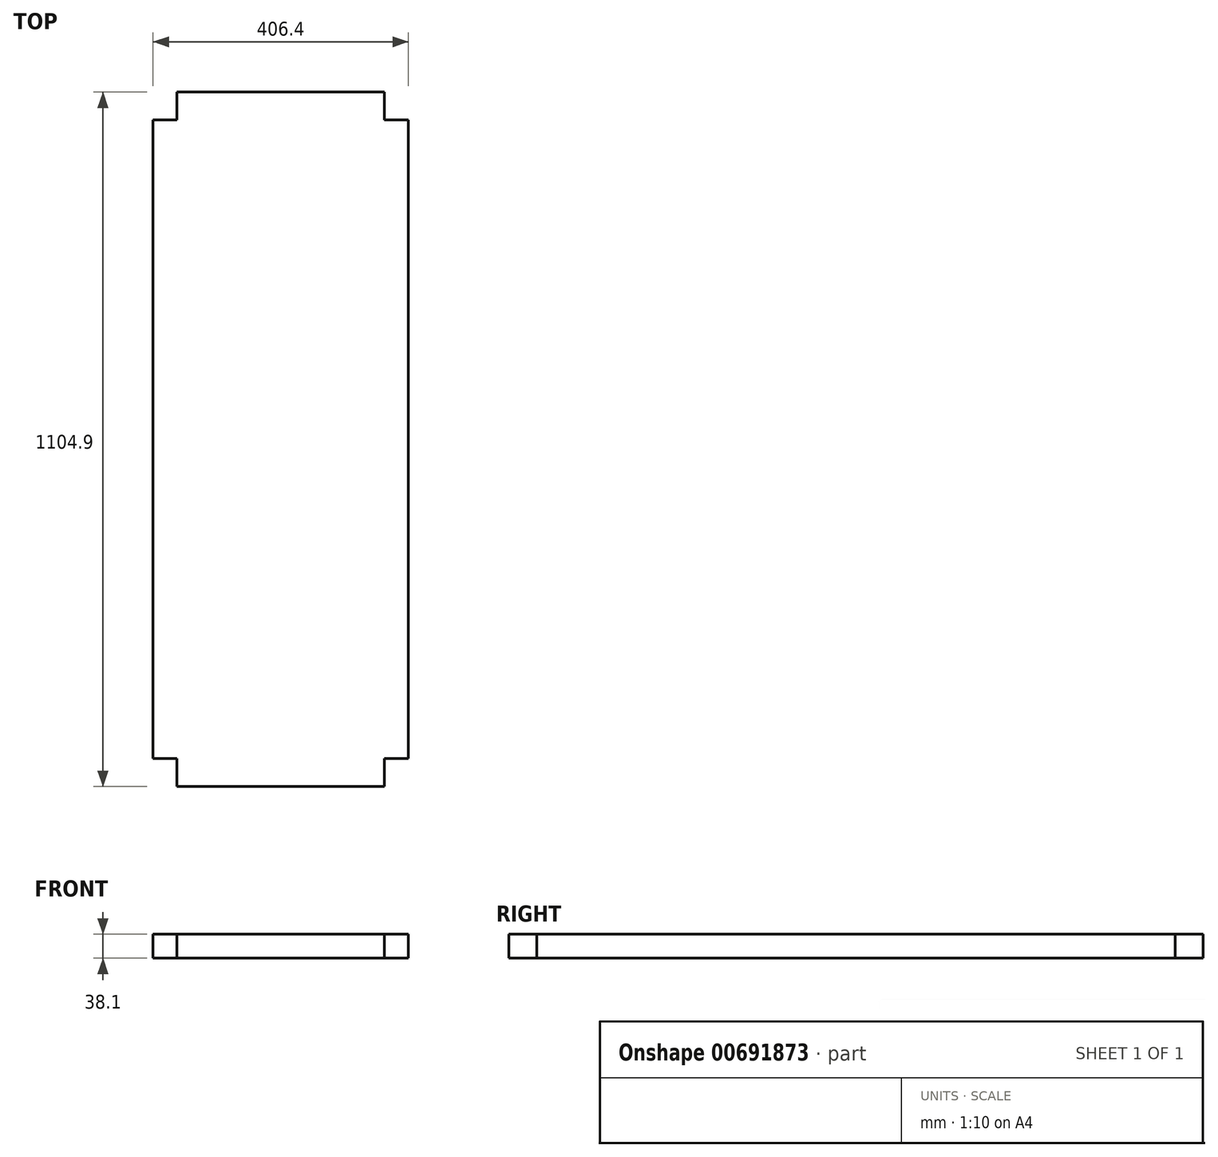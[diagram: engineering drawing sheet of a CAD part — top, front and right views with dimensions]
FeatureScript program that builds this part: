
annotation { "Feature Type Name" : "Feature", "Feature Type Description" : "" }
export const myFeature = defineFeature(function(context is Context, id is Id, definition is map)
    precondition{}
    {
        {
            var Q0;
            Q0=qCreatedBy(makeId("Top.planeOp"),FACE);
            var sketch = newSketch(context, id + "F0", { "sketchPlane" : qUnion([Q0])});
            skLineSegment(sketch, "E0.bottom", {"start": v(0, 0) * mm, "end": v(406.4, 0) * mm, "construction": true});
            skLineSegment(sketch, "E0.top", {"start": v(0, 1295.4) * mm, "end": v(406.4, 1295.4) * mm, "construction": true});
            skLineSegment(sketch, "E0.left", {"start": v(0, 0) * mm, "end": v(0, 1295.4) * mm, "construction": true});
            skLineSegment(sketch, "E0.right", {"start": v(406.4, 0) * mm, "end": v(406.4, 1295.4) * mm, "construction": true});
            skLineSegment(sketch, "E1", {"start": v(0, 628.65) * mm, "end": v(406.4, 628.65) * mm, "construction": true});
            skLineSegment(sketch, "E2", {"start": v(406.4, 717.55) * mm, "end": v(0, 717.55) * mm, "construction": true});
            skLineSegment(sketch, "E3", {"start": v(0, 50.8) * mm, "end": v(406.4, 50.8) * mm, "construction": true});
            skLineSegment(sketch, "E4", {"start": v(0, 1244.6) * mm, "end": v(406.4, 1244.6) * mm, "construction": true});
            skLineSegment(sketch, "E5", {"start": v(0, 1155.7) * mm, "end": v(406.4, 1155.7) * mm, "construction": true});
            skLineSegment(sketch, "E6", {"start": v(0, 139.7) * mm, "end": v(406.4, 139.7) * mm, "construction": true});
            skLineSegment(sketch, "E7", {"start": v(368.3, 1244.6) * mm, "end": v(368.3, 50.8) * mm, "construction": true});
            skLineSegment(sketch, "E8", {"start": v(0, 1200.15) * mm, "end": v(368.3, 1200.15) * mm, "construction": true});
            skLineSegment(sketch, "E9", {"start": v(0, 95.25) * mm, "end": v(368.3, 95.25) * mm, "construction": true});
            skLineSegment(sketch, "E10", {"start": v(38.1, 1295.4) * mm, "end": v(38.1, 0) * mm, "construction": true});
            skLineSegment(sketch, "E11", {"start": v(0, 717.55) * mm, "end": v(0, 1155.7) * mm});
            skLineSegment(sketch, "E12", {"start": v(38.1, 1155.7) * mm, "end": v(38.1, 1200.15) * mm});
            skLineSegment(sketch, "E13", {"start": v(38.1, 1200.15) * mm, "end": v(368.3, 1200.15) * mm});
            skLineSegment(sketch, "E14", {"start": v(368.3, 1155.7) * mm, "end": v(406.4, 1155.7) * mm});
            skLineSegment(sketch, "E15", {"start": v(406.4, 717.55) * mm, "end": v(368.3, 717.55) * mm});
            skLineSegment(sketch, "E16", {"start": v(368.3, 717.55) * mm, "end": v(368.3, 628.65) * mm});
            skLineSegment(sketch, "E17", {"start": v(368.3, 628.65) * mm, "end": v(406.4, 628.65) * mm});
            skLineSegment(sketch, "E18", {"start": v(0, 1155.7) * mm, "end": v(38.1, 1155.7) * mm});
            skLineSegment(sketch, "E19", {"start": v(368.3, 1200.15) * mm, "end": v(368.3, 1155.7) * mm});
            skLineSegment(sketch, "E20", {"start": v(406.4, 1155.7) * mm, "end": v(406.4, 717.55) * mm});
            skLineSegment(sketch, "E21", {"start": v(406.4, 628.65) * mm, "end": v(406.4, 139.7) * mm});
            skLineSegment(sketch, "E22", {"start": v(406.4, 139.7) * mm, "end": v(368.3, 139.7) * mm});
            skLineSegment(sketch, "E23", {"start": v(368.3, 139.7) * mm, "end": v(368.3, 95.25) * mm});
            skLineSegment(sketch, "E24", {"start": v(368.3, 95.25) * mm, "end": v(38.1, 95.25) * mm});
            skLineSegment(sketch, "E25", {"start": v(38.1, 95.25) * mm, "end": v(38.1, 139.7) * mm});
            skLineSegment(sketch, "E26", {"start": v(38.1, 139.7) * mm, "end": v(0, 139.7) * mm});
            skLineSegment(sketch, "E27", {"start": v(0, 628.65) * mm, "end": v(0, 139.7) * mm});
            skLineSegment(sketch, "E28", {"start": v(0, 628.65) * mm, "end": v(38.1, 628.65) * mm});
            skLineSegment(sketch, "E29", {"start": v(38.1, 628.65) * mm, "end": v(38.1, 717.55) * mm});
            skLineSegment(sketch, "E30", {"start": v(38.1, 717.55) * mm, "end": v(0, 717.55) * mm});
            skLineSegment(sketch, "E31", {"start": v(0, 717.55) * mm, "end": v(0, 628.65) * mm});
            skLineSegment(sketch, "E32", {"start": v(406.4, 717.55) * mm, "end": v(406.4, 628.65) * mm});
            skSolve(sketch);
        }
        {
            var Q0;
            Q0=qSketchRegion(id+"F0",true);
            extrude(context, id + "F1", {"entities" : qUnion([Q0]), "depth" : 38.1 * mm, "offsetDistance" : 25.4 * mm});
        }
    });
